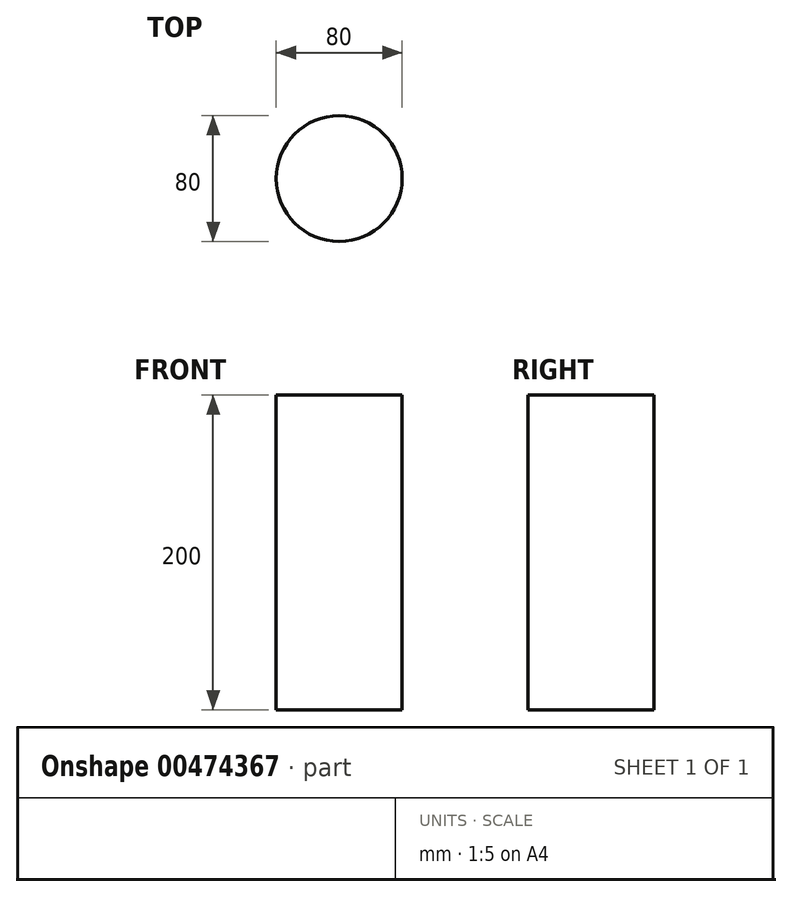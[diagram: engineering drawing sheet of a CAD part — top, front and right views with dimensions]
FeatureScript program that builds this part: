
annotation { "Feature Type Name" : "Feature", "Feature Type Description" : "" }
export const myFeature = defineFeature(function(context is Context, id is Id, definition is map)
    precondition{}
    {
        {
            var Q0;
            Q0=qCreatedBy(makeId("Top.planeOp"),FACE);
            var sketch = newSketch(context, id + "F0", { "sketchPlane" : qUnion([Q0])});
            skCircle(sketch, "E0", {"center": v(0, 0) * mm, "radius": 40 * mm});
            skSolve(sketch);
        }
        {
            var Q0;
            Q0 = qSketchRegion(id + "F0", true);
            extrude(context, id + "F1", {"entities" : qUnion([Q0]), "depth" : 200 * mm});
        }
    });
